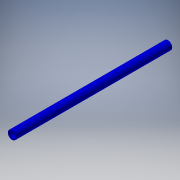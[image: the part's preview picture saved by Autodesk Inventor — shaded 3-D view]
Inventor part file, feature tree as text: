
AUTODESK INVENTOR PART (.ipt)
format: ipt  version: 2018.2 (Build 222227000, 227)  size: 105,984 bytes
history: native  units: in
note: dims shown in document units (in); Inventor stores cm internally (conversion verified against a paired STEP export)
features: extrude x1, sketch x1
ambient origin geometry x8: Origin, YZ Plane, XZ Plane, XY Plane, X Axis, Y Axis, Z Axis, Center Point
bodies: Solid1 (feature_tree)
feature tree (2):
  extrude  "Extrusion1"  Depth=24.0in
  sketch  "Sketch1"  dims[d0=1.315in d1=1.0in d2=24.0in d3=0.0in]
